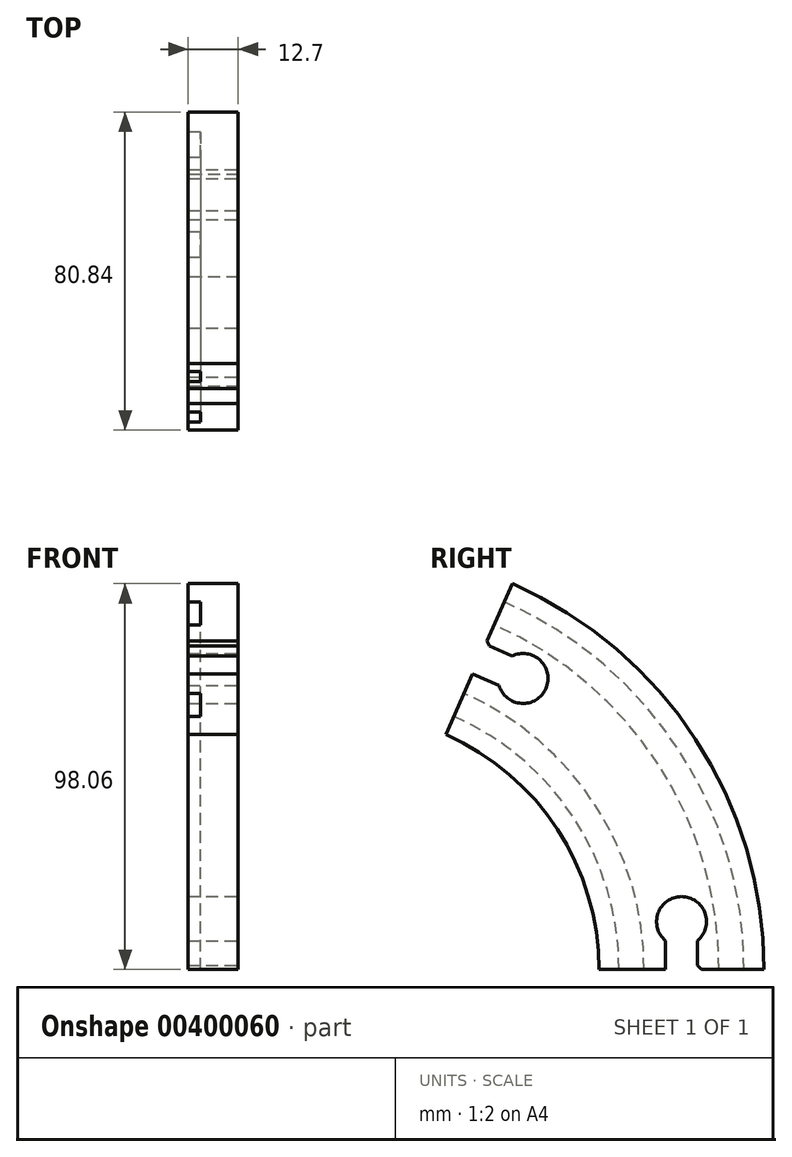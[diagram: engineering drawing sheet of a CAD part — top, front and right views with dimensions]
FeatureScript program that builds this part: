
annotation { "Feature Type Name" : "Feature", "Feature Type Description" : "" }
export const myFeature = defineFeature(function(context is Context, id is Id, definition is map)
    precondition{}
    {
        {
            var Q0;
            Q0=qCreatedBy(makeId("Top.planeOp"),FACE);
            var sketch = newSketch(context, id + "F0", { "sketchPlane" : qUnion([Q0])});
            skLineSegment(sketch, "E0", {"start": v(-2.98, -20.96) * mm, "end": v(-2.98, -15.88) * mm});
            skLineSegment(sketch, "E1", {"start": v(-2.98, -15.88) * mm, "end": v(0.2, -15.88) * mm});
            skLineSegment(sketch, "E2", {"start": v(0.2, -15.88) * mm, "end": v(0.2, -9.53) * mm});
            skLineSegment(sketch, "E3", {"start": v(0.2, -9.53) * mm, "end": v(-2.98, -9.53) * mm});
            skLineSegment(sketch, "E4", {"start": v(-2.98, -9.52) * mm, "end": v(-2.98, 9.52) * mm});
            skLineSegment(sketch, "E5", {"start": v(-2.98, 9.53) * mm, "end": v(0.2, 9.53) * mm});
            skLineSegment(sketch, "E6", {"start": v(0.2, 9.53) * mm, "end": v(0.2, 15.88) * mm});
            skLineSegment(sketch, "E7", {"start": v(0.2, 15.88) * mm, "end": v(-2.98, 15.88) * mm});
            skLineSegment(sketch, "E8", {"start": v(-2.98, 15.88) * mm, "end": v(-2.98, 20.96) * mm});
            skLineSegment(sketch, "E9", {"start": v(-2.98, 20.96) * mm, "end": v(9.72, 20.96) * mm});
            skLineSegment(sketch, "E10", {"start": v(9.72, 20.96) * mm, "end": v(9.72, -20.96) * mm});
            skLineSegment(sketch, "E11", {"start": v(9.72, -20.96) * mm, "end": v(-2.98, -20.96) * mm});
            skLineSegment(sketch, "E12", {"start": v(9.72, 0) * mm, "end": v(-14.33, 0) * mm, "construction": true});
            skSolve(sketch);
        }
        {
            var Q0;
            Q0=qCreatedBy(makeId("Right.planeOp"),FACE);
            var sketch = newSketch(context, id + "F1", { "sketchPlane" : qUnion([Q0])});
            skArc(sketch, "E13", {"start": v(0, 0) * mm, "mid": v(-13.99, 47.08) * mm, "end": v(-51.42, 78.89) * mm});
            skLineSegment(sketch, "E14", {"start": v(0, 0) * mm, "end": v(0, 24.38) * mm, "construction": true});
            skSolve(sketch);
        }
        {
            var Q0;
            Q0 = qSketchRegion(id + "F0", true);
            var Q1;
            Q1=sQuery(id+"F1.wireOp",EDGE,"E13");
            sweep(context, id + "F2", {"profiles" : qUnion([Q0]), "path" : qUnion([Q1])});
        }
        {
            var Q0;
            Q0=makeQuery(id+"F2.opSweep","SWEPT_FACE",FACE,{"disambiguationData":[OSD([sQuery(id+"F0.wireOp",EDGE,"E10"),sQuery(id+"F1.wireOp",EDGE,"E13")])]});
            var sketch = newSketch(context, id + "F3", { "sketchPlane" : qUnion([Q0])});
            skLineSegment(sketch, "E15", {"start": v(-51.42, 78.89) * mm, "end": v(-35.14, 71.7) * mm, "construction": true});
            skLineSegment(sketch, "E16", {"start": v(0, 0) * mm, "end": v(0, 26.47) * mm, "construction": true});
            skPoint(sketch, "E16.endSnap0", {"position": v(0, 0) * mm});
            skLineSegment(sketch, "E17", {"start": v(-4.06, 0) * mm, "end": v(-4.06, 7.31) * mm});
            skLineSegment(sketch, "E18", {"start": v(4.06, 0) * mm, "end": v(4.06, 7.31) * mm});
            skArc(sketch, "E19", {"start": v(4.06, 7.31) * mm, "mid": v(0, 18.54) * mm, "end": v(-4.06, 7.31) * mm});
            skLineSegment(sketch, "E20", {"start": v(-4.06, 0) * mm, "end": v(4.06, 0) * mm});
            skLineSegment(sketch, "E21", {"start": v(-49.78, 82.6) * mm, "end": v(-43.09, 79.65) * mm});
            skLineSegment(sketch, "E22", {"start": v(-53.06, 75.17) * mm, "end": v(-46.37, 72.22) * mm});
            skArc(sketch, "E23", {"start": v(-46.37, 72.22) * mm, "mid": v(-34.45, 71.4) * mm, "end": v(-43.09, 79.65) * mm});
            skLineSegment(sketch, "E24", {"start": v(-49.78, 82.6) * mm, "end": v(-53.06, 75.17) * mm});
            skSolve(sketch);
        }
        {
            var Q0;
            Q0 = qSketchRegion(id + "F3", true);
            extrude(context, id + "F4", {"entities" : qUnion([Q0]), "operationType" : NewBodyOperationType.REMOVE, "endBound" : BoundingType.UP_TO_NEXT, "oppositeDirection" : true, "depth" : 25.4 * mm});
        }
        {
            var Q0;
            Q0=makeQuery(id+"F4.boolean.opBoolean","COPY",EDGE,{"derivedFrom":makeQuery(id+"F4.opExtrude","SWEPT_EDGE",EDGE,{"disambiguationData":[OSD([sQuery(id+"F0.wireOp",EDGE,"E10"),sQuery(id+"F1.wireOp",VERTEX,"E13.end"),sQuery(id+"F3.wireOp",EDGE,"E22"),sQuery(id+"F3.wireOp",EDGE,"E24")])]})});
            var Q1;
            Q1=makeQuery(id+"F4.boolean.opBoolean","COPY",EDGE,{"derivedFrom":makeQuery(id+"F4.opExtrude","SWEPT_EDGE",EDGE,{"disambiguationData":[OSD([sQuery(id+"F0.wireOp",EDGE,"E10"),sQuery(id+"F1.wireOp",VERTEX,"E13.end"),sQuery(id+"F3.wireOp",EDGE,"E21"),sQuery(id+"F3.wireOp",EDGE,"E24")])]})});
            var Q2;
            Q2=makeQuery(id+"F4.boolean.opBoolean","COPY",EDGE,{"derivedFrom":makeQuery(id+"F4.opExtrude","SWEPT_EDGE",EDGE,{"disambiguationData":[OSD([sQuery(id+"F0.wireOp",EDGE,"E10"),sQuery(id+"F1.wireOp",VERTEX,"E13.start"),sQuery(id+"F3.wireOp",EDGE,"E18"),sQuery(id+"F3.wireOp",EDGE,"E20")])]})});
            var Q3;
            Q3=makeQuery(id+"F4.boolean.opBoolean","COPY",EDGE,{"derivedFrom":makeQuery(id+"F4.opExtrude","SWEPT_EDGE",EDGE,{"disambiguationData":[OSD([sQuery(id+"F0.wireOp",EDGE,"E10"),sQuery(id+"F1.wireOp",VERTEX,"E13.start"),sQuery(id+"F3.wireOp",EDGE,"E17"),sQuery(id+"F3.wireOp",EDGE,"E20")])]})});
            chamfer(context, id + "F5", {"entities" : qUnion([Q0, Q1, Q2, Q3]), "width" : 1.02 * mm, "tangentPropagation" : true});
        }
    });
